# Revit family: QF_Southern Pride_SPK-500
name_source: partatom
category: Specialty Equipment
units: mm (PartAtom-declared; Revit-internal decimal feet)

## family parameters
Always vertical = Yes
Cut with Voids When Loaded = No
Maintain Annotation Orientation = No
OmniClass Number = 23.40.40.00
OmniClass Title = Food Service Equipment and Furnishings
Part Type = Normal
Room Calculation Point = No
Round Connector Dimension = Use Diameter
Shared = No
Work Plane-Based = No

## types (1)
- QF_Southern Pride_SPK-500
    Apparent Power = 1800 VA
    Assembly Code = E1090320
    Box Height = 52.125 "
    CSI MasterFormat = 11 44 00
    Conn Plug = NEMA 5-15P
    Cycle = 60 Hz
    Default Elevation = 0 "
    Depth = 65.625 "
    Description = Rotisserie Smoker, Gas-Fired Wood Burning
    Door Height = 22 "
    Door Width = 46.875 "
    Elec Conn Connection Height = 52.875 "
    FL Amps = 15 A
    Foodservice Equipment Identifier = Yes
    Gas Connection Height = 30.625 "
    Gas Input = 75000.0 Btu/h
    Gas KW = 22
    Gas Size = 1"
    Indirect Waste Connection Height = 15.25 "
    Indirect Waste Size = 2"
    Leg Height = 19 "
    Manufacturer = Southern Pride
    Model = SPK-500
    Phase = 1
    URL = www.southernpride.com
    URL Cutsheet = https://www.southernpride.com
    Volts = 120 V
    Weight in Pounds = 1204
    Width = 52.5 "

## geometry (parser evidence)
native form markers: Blend x4, Sweep x12
no freeform markers — native parametric forms only
